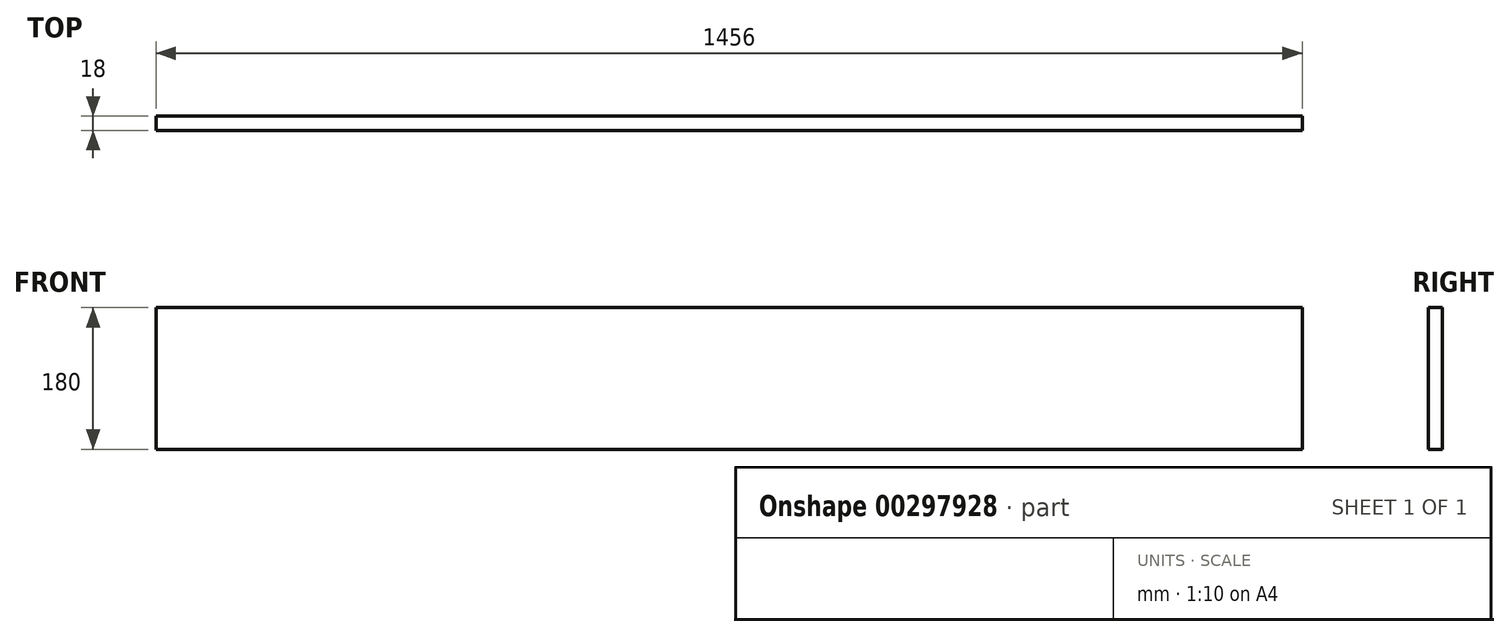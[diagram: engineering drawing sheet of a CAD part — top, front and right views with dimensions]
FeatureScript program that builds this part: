
annotation { "Feature Type Name" : "Feature", "Feature Type Description" : "" }
export const myFeature = defineFeature(function(context is Context, id is Id, definition is map)
    precondition{}
    {
        {
            var Q0;
            Q0=qCreatedBy(makeId("Front.planeOp"),FACE);
            var sketch = newSketch(context, id + "F0", { "sketchPlane" : qUnion([Q0])});
            skLineSegment(sketch, "E0.bottom", {"start": v(-721.1, 67.33) * mm, "end": v(734.9, 67.33) * mm});
            skLineSegment(sketch, "E0.top", {"start": v(-721.1, -112.67) * mm, "end": v(734.9, -112.67) * mm});
            skLineSegment(sketch, "E0.left", {"start": v(-721.1, 67.33) * mm, "end": v(-721.1, -112.67) * mm});
            skLineSegment(sketch, "E0.right", {"start": v(734.9, 67.33) * mm, "end": v(734.9, -112.67) * mm});
            skSolve(sketch);
        }
        {
            var Q0;
            Q0=makeQuery(id+"F0.imprint","IMPRINT",FACE,{"disambiguationData":[TD([[makeQuery(id+"F0.imprint","IMPRINT",EDGE,{"derivedFrom":sQuery(id+"F0.wireOp",EDGE,"E0.bottom")}),-1.0]])]});
            extrude(context, id + "F1", {"entities" : qUnion([Q0]), "endBound" : BoundingType.SYMMETRIC, "depth" : 18 * mm});
        }
    });
